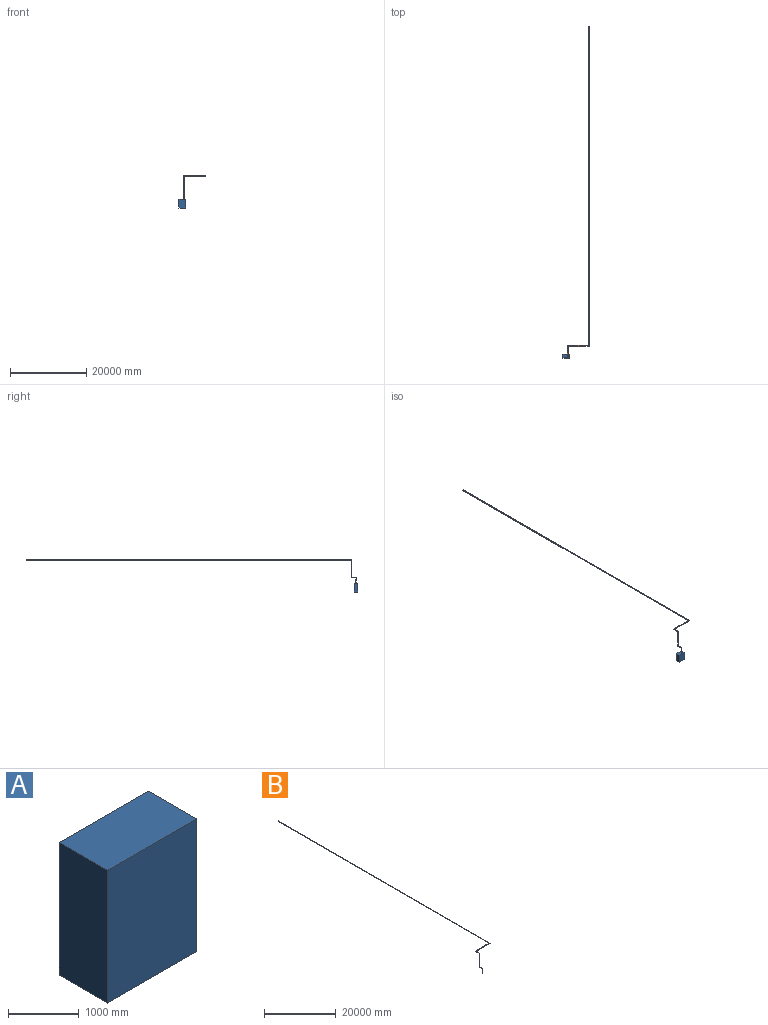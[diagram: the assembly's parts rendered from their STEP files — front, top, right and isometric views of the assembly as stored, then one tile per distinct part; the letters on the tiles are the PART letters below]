
ASSEMBLY  parts=2 mates=1
PART A: 6 faces, bbox 1778x965.2x2286 mm
  f0: plane 2286x1778mm, normal (0,1,0), area 4064508mm2, adj f1,f3,f4,f5
  f1: plane 2286x965.2mm, normal (-1,0,0), area 2206447.2mm2, adj f0,f2,f4,f5
  f2: plane 2286x1778mm, normal (0,-1,0), area 4064508mm2, adj f1,f3,f4,f5
  f3: plane 2286x965.2mm, normal (1,0,0), area 2206447.2mm2, adj f0,f2,f4,f5
  f4: plane 1778x965.2mm, normal (0,0,1), area 1716125.6mm2, adj f0,f1,f2,f3
  f5: plane 1778x965.2mm, normal (0,0,-1), area 1716125.6mm2, adj f0,f1,f2,f3
PART B: 16 faces, bbox 5656.6x86385.4x6096 mm
  f0: plane 1219.2x170.18mm, normal (0,0,1), area 207483.5mm2, adj f2,f3,f4,f8
  f1: plane 1397x170.18mm, normal (0,1,0), area 237741.5mm2, adj f2,f4,f5,f6
  f2: plane 6096x2870.2mm, normal (-1,0,0), area 1122578.4mm2, adj f0,f1,f3,f5,f6,f7,f8,f9
  f3: plane 1524x170.18mm, normal (0,-1,0), area 259354.3mm2, adj f0,f2,f4,f5
  f4: plane 6096x2700.02mm, normal (1,0,0), area 1100965.5mm2, adj f0,f1,f3,f5,f6,f7,f8,f9
  f5: plane 170.18x127mm, normal (0,0,-1), area 21612.9mm2, adj f1,f2,f3,f4
  f6: plane 1219.2x170.18mm, normal (0,0,-1), area 207483.5mm2, adj f1,f2,f4,f7
  f7: plane 4572x170.18mm, normal (0,1,0), area 778063mm2, adj f2,f4,f6,f10
  f8: plane 4572x170.18mm, normal (0,-1,0), area 778063mm2, adj f0,f2,f4,f9
  f9: plane 85166.2x5656.58mm, normal (0,0,1), area 15427259.5mm2, adj f2,f4,f8,f11,f12,f13,f14,f15
  f10: plane 85039.2x5656.58mm, normal (0,0,-1), area 15405646.6mm2, adj f2,f4,f7,f11,f12,f13,f14,f15
  f11: plane 5486.4x127mm, normal (0,1,0), area 696772.8mm2, adj f2,f9,f10,f14
  f12: plane 5486.4x127mm, normal (0,-1,0), area 696772.8mm2, adj f4,f9,f10,f13
  f13: plane 83685.38x127mm, normal (1,0,0), area 10628043.3mm2, adj f9,f10,f12,f15
  f14: plane 83515.2x127mm, normal (-1,0,0), area 10606430.4mm2, adj f9,f10,f11,f15
  f15: plane 170.18x127mm, normal (0,1,0), area 21612.9mm2, adj f9,f10,f13,f14
PLACE A at identity
PLACE B t=(1210.31,419.1,2286)mm
MATE fastened B.f5 <-> A.f4  axis (0,0,-1) through (1295.4,482.6,2286)mm
